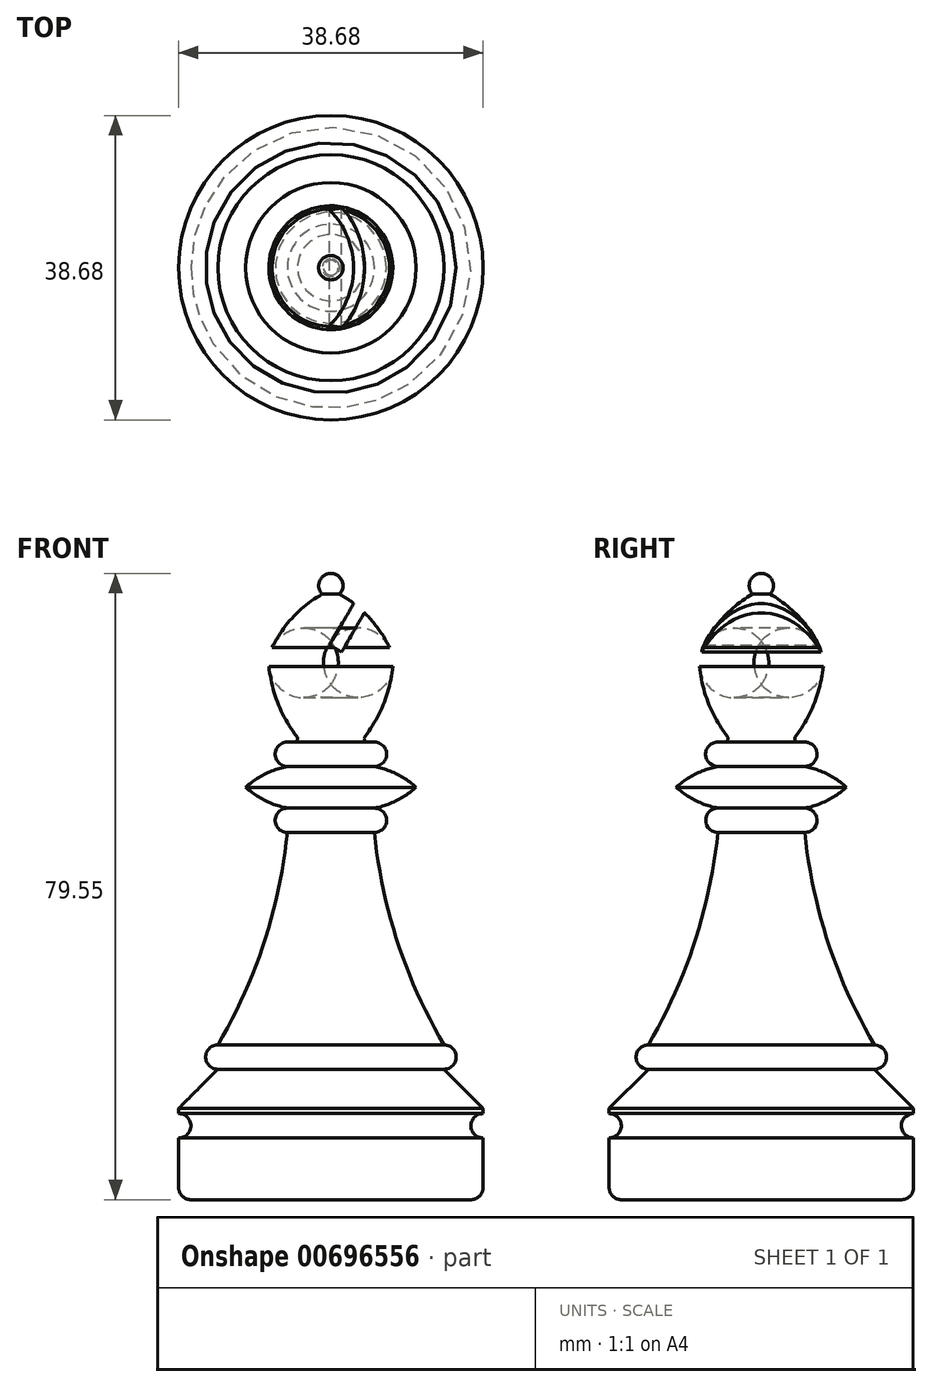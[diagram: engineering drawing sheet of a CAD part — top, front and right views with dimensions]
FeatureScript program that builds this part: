
annotation { "Feature Type Name" : "Feature", "Feature Type Description" : "" }
export const myFeature = defineFeature(function(context is Context, id is Id, definition is map)
    precondition{}
    {
        {
            var Q0;
            Q0=qCreatedBy(makeId("Front.planeOp"),FACE);
            var sketch = newSketch(context, id + "F0", { "sketchPlane" : qUnion([Q0])});
            skLineSegment(sketch, "E0", {"start": v(0, 0) * mm, "end": v(16.51, 0) * mm});
            skLineSegment(sketch, "E1", {"start": v(16.51, 0) * mm, "end": v(22.22, -5.71) * mm});
            skLineSegment(sketch, "E2", {"start": v(22.22, -5.71) * mm, "end": v(22.22, -6.48) * mm});
            skArc(sketch, "E3", {"start": v(22.22, -6.48) * mm, "mid": v(20.45, -8.25) * mm, "end": v(22.23, -10.03) * mm});
            skLineSegment(sketch, "E4", {"start": v(22.23, -10.03) * mm, "end": v(22.23, -19.05) * mm});
            skLineSegment(sketch, "E5", {"start": v(22.23, -19.05) * mm, "end": v(0, -19.05) * mm});
            skLineSegment(sketch, "E6", {"start": v(0, -19.05) * mm, "end": v(0, 0) * mm});
            skSolve(sketch);
        }
        {
            var Q0;
            Q0=makeQuery(id+"F0.imprint","IMPRINT",FACE,{"disambiguationData":[TD([[makeQuery(id+"F0.imprint","IMPRINT",EDGE,{"derivedFrom":sQuery(id+"F0.wireOp",EDGE,"E0")}),-1.0]])]});
            var Q1;
            Q1=sQuery(id+"F0.wireOp",EDGE,"E6");
            revolve(context, id + "F1", {"entities" : qUnion([Q0]), "axis" : qUnion([Q1]), "revolveType" : RevolveType.FULL});
        }
        {
            var Q0;
            Q0=makeQuery(id+"F1.opRevolve","SWEPT_EDGE",EDGE,{"disambiguationData":[OSD([sQuery(id+"F0.wireOp",EDGE,"E4"),sQuery(id+"F0.wireOp",EDGE,"E5")])]});
            fillet(context, id + "F2", {"entities" : qUnion([Q0]), "radius" : 1.78 * mm, "tangentPropagation" : true, "allowEdgeOverflow" : false});
        }
        {
            var Q0;
            Q0=qCreatedBy(makeId("Front.planeOp"),FACE);
            var sketch = newSketch(context, id + "F3", { "sketchPlane" : qUnion([Q0])});
            skLineSegment(sketch, "E7", {"start": v(0, 72.4) * mm, "end": v(0, 0) * mm});
            skLineSegment(sketch, "E8", {"start": v(0, 0) * mm, "end": v(16.51, 0) * mm});
            skArc(sketch, "E9", {"start": v(16.51, 0) * mm, "mid": v(18.29, 1.78) * mm, "end": v(16.51, 3.56) * mm});
            skArc(sketch, "E10", {"start": v(6.35, 34.57) * mm, "mid": v(9.75, 18.51) * mm, "end": v(16.51, 3.56) * mm});
            skArc(sketch, "E11", {"start": v(6.35, 34.57) * mm, "mid": v(8.13, 36.35) * mm, "end": v(6.35, 38.13) * mm});
            skArc(sketch, "E12", {"start": v(6.35, 38.13) * mm, "mid": v(9.6, 39.23) * mm, "end": v(12.45, 41.17) * mm});
            skArc(sketch, "E13", {"start": v(12.45, 41.17) * mm, "mid": v(9.6, 43.11) * mm, "end": v(6.35, 44.22) * mm});
            skArc(sketch, "E14", {"start": v(6.35, 44.22) * mm, "mid": v(8.13, 46) * mm, "end": v(6.35, 47.78) * mm});
            skArc(sketch, "E15", {"start": v(9.14, 60.22) * mm, "mid": v(6, 65.48) * mm, "end": v(1.27, 69.37) * mm});
            skArc(sketch, "E16", {"start": v(1.27, 69.37) * mm, "mid": v(1.64, 71.3) * mm, "end": v(0, 72.4) * mm});
            skLineSegment(sketch, "E17", {"start": v(6.35, 38.13) * mm, "end": v(6.35, 44.22) * mm, "construction": true});
            skLineSegment(sketch, "E18", {"start": v(6.35, 41.17) * mm, "end": v(12.45, 41.17) * mm, "construction": true});
            skArc(sketch, "E19", {"start": v(4.32, 47.78) * mm, "mid": v(7.78, 53.6) * mm, "end": v(9.14, 60.22) * mm});
            skLineSegment(sketch, "E20", {"start": v(4.32, 47.78) * mm, "end": v(6.35, 47.78) * mm});
            skPoint(sketch, "E21", {"position": v(4.12, 67.37) * mm});
            skLineSegment(sketch, "E22", {"start": v(4.12, 67.37) * mm, "end": v(0, 60.22) * mm, "construction": true});
            skSolve(sketch);
        }
        {
            var Q0;
            Q0=qSketchRegion(id+"F3",true);
            var Q1;
            Q1=sQuery(id+"F3.wireOp",EDGE,"E7");
            revolve(context, id + "F4", {"operationType" : NewBodyOperationType.ADD, "entities" : qUnion([Q0]), "axis" : qUnion([Q1]), "revolveType" : RevolveType.FULL});
        }
        {
            var Q0;
            Q0=makeQuery(id+"F4.opRevolve","SWEPT_EDGE",EDGE,{"disambiguationData":[OSD([sQuery(id+"F3.wireOp",EDGE,"E15"),sQuery(id+"F3.wireOp",EDGE,"E19")])]});
            fillet(context, id + "F5", {"entities" : qUnion([Q0]), "radius" : 5.08 * mm, "tangentPropagation" : true, "allowEdgeOverflow" : false});
        }
        {
            var Q0;
            Q0=makeQuery(id+"F4.opRevolve","SWEPT_EDGE",EDGE,{"disambiguationData":[OSD([sQuery(id+"F3.wireOp",EDGE,"E19"),sQuery(id+"F3.wireOp",EDGE,"E20")])]});
            fillet(context, id + "F6", {"entities" : qUnion([Q0]), "radius" : 0.5 * mm, "tangentPropagation" : true, "allowEdgeOverflow" : false});
        }
        {
            var Q0;
            Q0=sQuery(id+"F3.wireOp",VERTEX,"E21");
            var Q1;
            Q1=sQuery(id+"F3.wireOp",EDGE,"E22");
            cPlane(context, id + "F7", {"entities" : qUnion([Q0, Q1]), "cplaneType" : CPlaneType.LINE_POINT, "offset" : 25.4 * mm, "width" : 152.4 * mm, "height" : 152.4 * mm});
        }
        {
            var Q0;
            Q0=qCreatedBy(id+"F7.planeOp",FACE);
            var sketch = newSketch(context, id + "F8", { "sketchPlane" : qUnion([Q0])});
            skLineSegment(sketch, "E23.bottom", {"start": v(-29.1, 12.7) * mm, "end": v(-31.13, 12.7) * mm});
            skLineSegment(sketch, "E23.top", {"start": v(-29.1, -12.7) * mm, "end": v(-31.13, -12.7) * mm});
            skLineSegment(sketch, "E23.left", {"start": v(-29.1, 12.7) * mm, "end": v(-29.1, -12.7) * mm});
            skLineSegment(sketch, "E23.right", {"start": v(-31.13, 12.7) * mm, "end": v(-31.13, -12.7) * mm});
            skPoint(sketch, "E23.middle", {"position": v(-30.11, 0) * mm});
            skSolve(sketch);
        }
        {
            var Q0;
            Q0=qSketchRegion(id+"F8",true);
            var Q1;
            Q1=qCreatedBy(id+"FaZgaIPp9X6yMJz_1.planeOp",FACE);
            extrude(context, id + "F9", {"entities" : qUnion([Q0]), "operationType" : NewBodyOperationType.REMOVE, "oppositeDirection" : true, "depth" : 2.54 * mm, "hasSecondDirection" : true, "secondDirectionOppositeDirection" : false, "secondDirectionBoundEntityFace" : qUnion([Q1]), "secondDirectionDepth" : 6.86 * mm});
        }
        {
            var Q0;
            Q0=makeQuery(id+"F1.opRevolve","SWEPT_BODY",BODY,{"disambiguationData":[OSD([sQuery(id+"F0.wireOp",EDGE,"E0"),sQuery(id+"F0.wireOp",EDGE,"E1"),sQuery(id+"F0.wireOp",EDGE,"E2"),sQuery(id+"F0.wireOp",EDGE,"E3"),sQuery(id+"F0.wireOp",EDGE,"E4"),sQuery(id+"F0.wireOp",EDGE,"E5"),sQuery(id+"F0.wireOp",EDGE,"E6")])]});
            var Q1;
            Q1=qCreatedBy(makeId("Origin.pointOp"),VERTEX);
            transform(context, id + "F10", {"entities" : qUnion([Q0]), "transformType" : TransformType.SCALE_UNIFORMLY, "scale" : .87, "scalePoint" : qUnion([Q1]), "makeCopy" : false});
        }
    });
